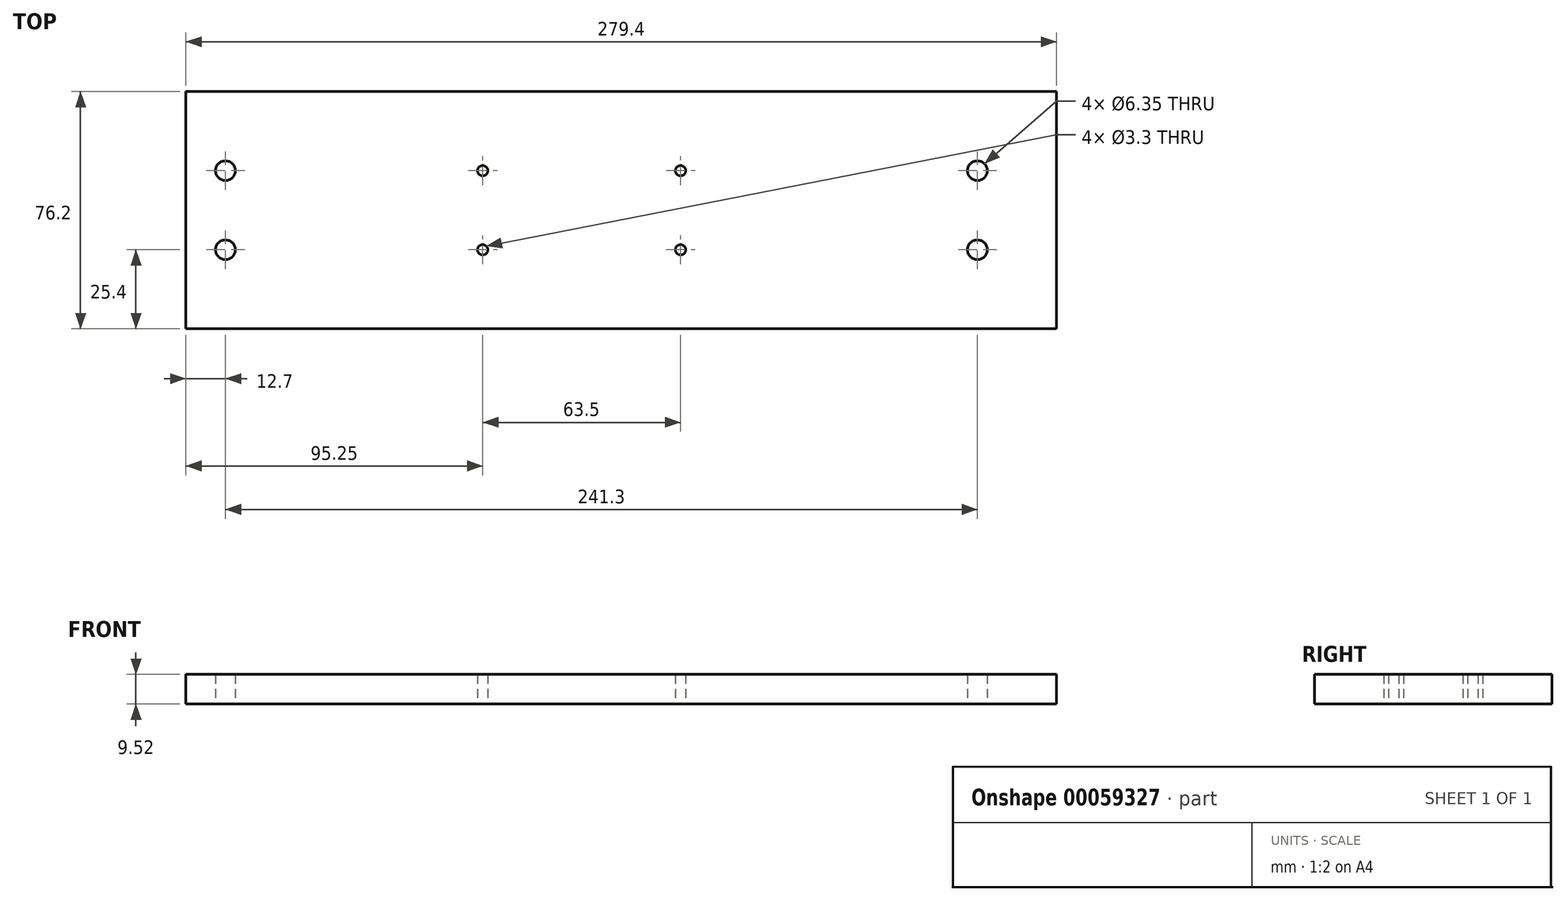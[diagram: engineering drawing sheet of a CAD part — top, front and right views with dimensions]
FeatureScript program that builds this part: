
annotation { "Feature Type Name" : "Feature", "Feature Type Description" : "" }
export const myFeature = defineFeature(function(context is Context, id is Id, definition is map)
    precondition{}
    {
        {
            var Q0;
            Q0=qCreatedBy(makeId("Top.planeOp"),FACE);
            var sketch = newSketch(context, id + "F0", { "sketchPlane" : qUnion([Q0])});
            skLineSegment(sketch, "E0.rect.bottom", {"start": v(-139.7, 38.1) * mm, "end": v(139.7, 38.1) * mm});
            skLineSegment(sketch, "E0.rect.top", {"start": v(-139.7, -38.1) * mm, "end": v(139.7, -38.1) * mm});
            skLineSegment(sketch, "E0.rect.left", {"start": v(-139.7, 38.1) * mm, "end": v(-139.7, -38.1) * mm});
            skLineSegment(sketch, "E0.rect.right", {"start": v(139.7, 38.1) * mm, "end": v(139.7, -38.1) * mm});
            skPoint(sketch, "E0.rect.middle", {"position": v(0, 0) * mm});
            skCircle(sketch, "E1", {"center": v(-127, 12.7) * mm, "radius": 3.18 * mm});
            skCircle(sketch, "E2", {"center": v(-44.45, 12.7) * mm, "radius": 1.65 * mm});
            skCircle(sketch, "E3", {"center": v(19.05, 12.7) * mm, "radius": 1.65 * mm});
            skCircle(sketch, "E4", {"center": v(114.3, 12.7) * mm, "radius": 3.18 * mm});
            skCircle(sketch, "E5.MirrorC", {"center": v(-44.45, -12.7) * mm, "radius": 1.65 * mm});
            skCircle(sketch, "E6.MirrorC", {"center": v(19.05, -12.7) * mm, "radius": 1.65 * mm});
            skCircle(sketch, "E7.MirrorC", {"center": v(114.3, -12.7) * mm, "radius": 3.18 * mm});
            skCircle(sketch, "E8.MirrorC", {"center": v(-127, -12.7) * mm, "radius": 3.18 * mm});
            skSolve(sketch);
        }
        {
            var Q0;
            Q0 = qSketchRegion(id + "F0", true);
            extrude(context, id + "F1", {"entities" : qUnion([Q0]), "endBound" : BoundingType.SYMMETRIC, "depth" : 9.52 * mm});
        }
    });
